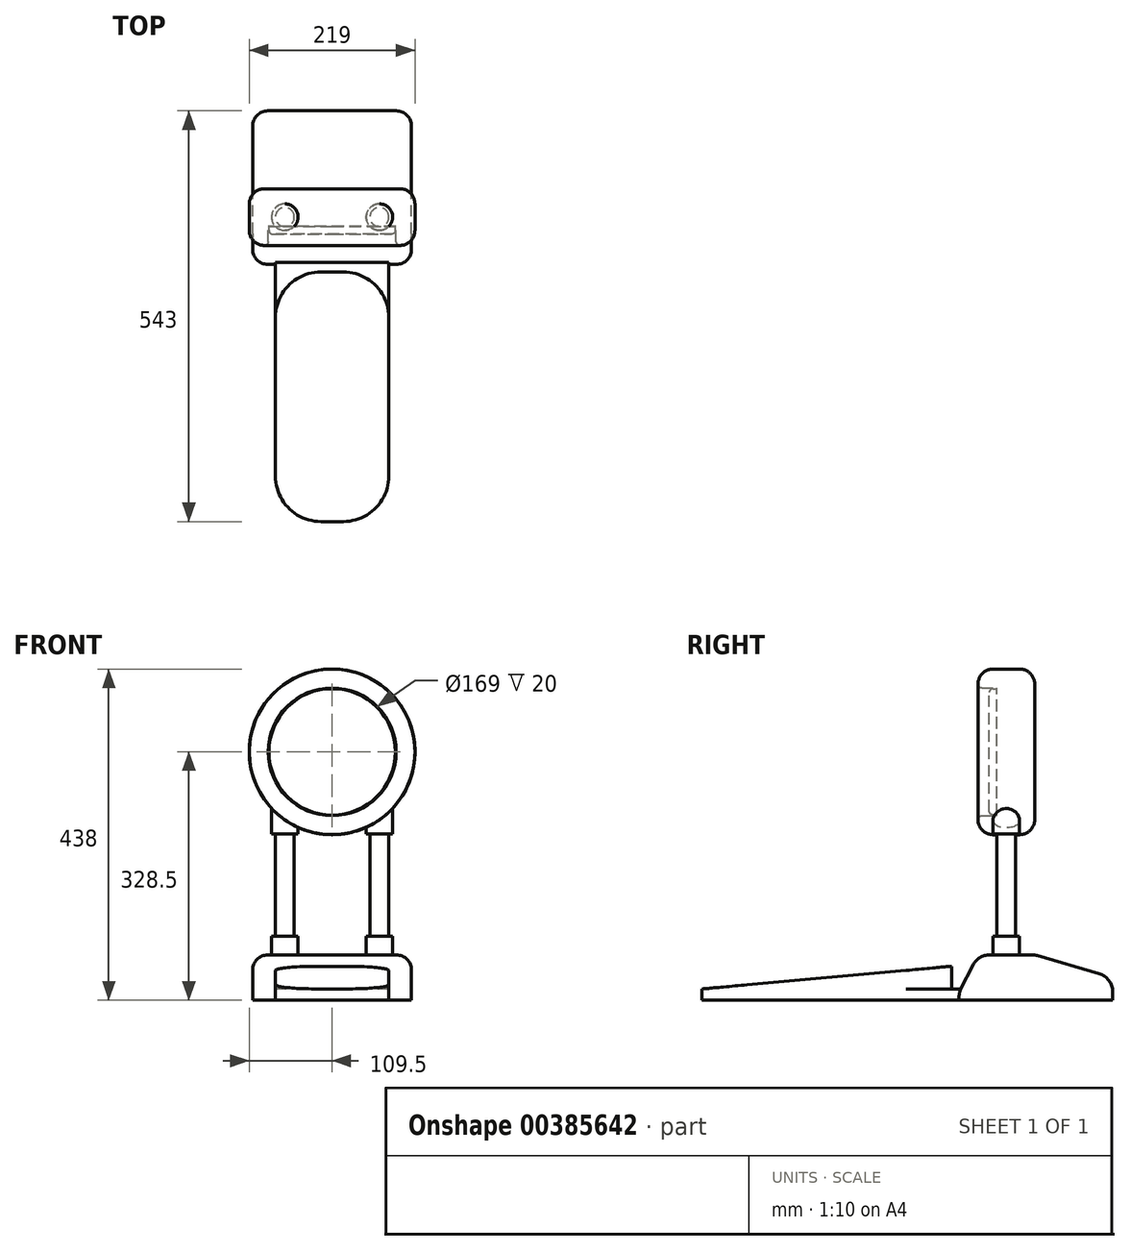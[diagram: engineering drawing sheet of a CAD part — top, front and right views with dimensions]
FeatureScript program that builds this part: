
annotation { "Feature Type Name" : "Feature", "Feature Type Description" : "" }
export const myFeature = defineFeature(function(context is Context, id is Id, definition is map)
    precondition{}
    {
        {
            var Q0;
            Q0=qCreatedBy(makeId("Front.planeOp"),FACE);
            var sketch = newSketch(context, id + "F0", { "sketchPlane" : qUnion([Q0])});
            skLineSegment(sketch, "E0.bottom", {"start": v(-109.5, 0) * mm, "end": v(109.5, 0) * mm, "construction": true});
            skLineSegment(sketch, "E0.top", {"start": v(-109.5, 438) * mm, "end": v(109.5, 438) * mm, "construction": true});
            skLineSegment(sketch, "E0.left", {"start": v(-109.5, 0) * mm, "end": v(-109.5, 438) * mm, "construction": true});
            skLineSegment(sketch, "E0.right", {"start": v(109.5, 0) * mm, "end": v(109.5, 438) * mm, "construction": true});
            skCircle(sketch, "E1", {"center": v(0, 328.5) * mm, "radius": 109.5 * mm});
            skCircle(sketch, "E2", {"center": v(0, 328.5) * mm, "radius": 83.5 * mm});
            skCircle(sketch, "E3", {"center": v(0, 328.5) * mm, "radius": 84.5 * mm});
            skSolve(sketch);
        }
        {
            var Q0;
            Q0=makeQuery(id+"F0.imprint","IMPRINT",FACE,{"disambiguationData":[TD([[makeQuery(id+"F0.imprint","IMPRINT",EDGE,{"derivedFrom":sQuery(id+"F0.wireOp",EDGE,"E1")}),1.0]])]});
            var Q1;
            Q1=makeQuery(id+"F0.imprint","IMPRINT",FACE,{"disambiguationData":[TD([[makeQuery(id+"F0.imprint","IMPRINT",EDGE,{"derivedFrom":sQuery(id+"F0.wireOp",EDGE,"E2")}),1.0]])]});
            var Q2;
            Q2=makeQuery(id+"F0.imprint","IMPRINT",FACE,{"disambiguationData":[TD([[makeQuery(id+"F0.imprint","IMPRINT",EDGE,{"derivedFrom":sQuery(id+"F0.wireOp",EDGE,"E2")}),-1.0]])]});
            extrude(context, id + "F1", {"entities" : qUnion([Q0, Q1, Q2]), "oppositeDirection" : true, "depth" : 50 * mm});
        }
        {
            var Q0;
            Q0=makeQuery(id+"F0.imprint","IMPRINT",FACE,{"disambiguationData":[TD([[makeQuery(id+"F0.imprint","IMPRINT",EDGE,{"derivedFrom":sQuery(id+"F0.wireOp",EDGE,"E2")}),1.0]])]});
            extrude(context, id + "F2", {"entities" : qUnion([Q0]), "operationType" : NewBodyOperationType.ADD, "depth" : 10 * mm});
        }
        {
            var Q0;
            Q0=makeQuery(id+"F0.imprint","IMPRINT",FACE,{"disambiguationData":[TD([[makeQuery(id+"F0.imprint","IMPRINT",EDGE,{"derivedFrom":sQuery(id+"F0.wireOp",EDGE,"E1")}),1.0]])]});
            extrude(context, id + "F3", {"entities" : qUnion([Q0]), "operationType" : NewBodyOperationType.ADD, "depth" : 25 * mm});
        }
        {
            var Q0;
            Q0=makeQuery(id+"F3.opExtrude","CAP_EDGE",EDGE,{"disambiguationData":[OSD([sQuery(id+"F0.wireOp",EDGE,"E1")])],"isStart":false});
            var Q1;
            Q1=makeQuery(id+"F1.opExtrude","CAP_EDGE",EDGE,{"disambiguationData":[OSD([sQuery(id+"F0.wireOp",EDGE,"E1")])],"isStart":false});
            fillet(context, id + "F4", {"entities" : qUnion([Q0, Q1]), "radius" : 20 * mm, "tangentPropagation" : true, "allowEdgeOverflow" : false});
        }
        {
            var Q0;
            Q0=makeQuery(id+"F3.opExtrude","CAP_EDGE",EDGE,{"disambiguationData":[OSD([sQuery(id+"F0.wireOp",EDGE,"E3")])],"isStart":false});
            fillet(context, id + "F5", {"entities" : qUnion([Q0]), "radius" : 5 * mm, "tangentPropagation" : true, "allowEdgeOverflow" : false});
        }
        {
            var Q0;
            Q0=makeQuery(id+"F2.opExtrude","CAP_EDGE",EDGE,{"disambiguationData":[OSD([sQuery(id+"F0.wireOp",EDGE,"E2")])],"isStart":false});
            fillet(context, id + "F6", {"entities" : qUnion([Q0]), "radius" : 5 * mm, "tangentPropagation" : true, "allowEdgeOverflow" : false});
        }
        {
            var Q0;
            Q0=qCreatedBy(makeId("Right.planeOp"),FACE);
            var sketch = newSketch(context, id + "F7", { "sketchPlane" : qUnion([Q0])});
            skLineSegment(sketch, "E4.bottom", {"start": v(-50, 0) * mm, "end": v(153, 0) * mm});
            skLineSegment(sketch, "E4.top", {"start": v(-25, 60) * mm, "end": v(50, 60) * mm});
            skLineSegment(sketch, "E4.left", {"start": v(-50, 0) * mm, "end": v(-50, 10) * mm});
            skLineSegment(sketch, "E4.right", {"start": v(153, 0) * mm, "end": v(153, 30) * mm});
            skLineSegment(sketch, "E5", {"start": v(-50, 10) * mm, "end": v(-25, 60) * mm});
            skLineSegment(sketch, "E6", {"start": v(50, 60) * mm, "end": v(153, 30) * mm});
            skSolve(sketch);
        }
        {
            var Q0;
            Q0=makeQuery(id+"F7.imprint","IMPRINT",FACE,{"disambiguationData":[TD([[makeQuery(id+"F7.imprint","IMPRINT",EDGE,{"derivedFrom":sQuery(id+"F7.wireOp",EDGE,"E4.bottom")}),1.0]])]});
            extrude(context, id + "F8", {"entities" : qUnion([Q0]), "depth" : 105 * mm, "hasSecondDirection" : true, "secondDirectionOppositeDirection" : true, "secondDirectionDepth" : 105 * mm});
        }
        {
            var Q0;
            Q0=makeQuery(id+"F8.opExtrude","SWEPT_FACE",FACE,{"disambiguationData":[OSD([sQuery(id+"F7.wireOp",EDGE,"E4.top")])]});
            var sketch = newSketch(context, id + "F9", { "sketchPlane" : qUnion([Q0])});
            skCircle(sketch, "E7", {"center": v(-62.5, 12.5) * mm, "radius": 17.5 * mm});
            skCircle(sketch, "E8", {"center": v(62.5, 12.5) * mm, "radius": 17.5 * mm});
            skLineSegment(sketch, "E9", {"start": v(-62.5, 12.5) * mm, "end": v(62.5, 12.5) * mm, "construction": true});
            skCircle(sketch, "E10", {"center": v(-62.5, 12.5) * mm, "radius": 12.5 * mm});
            skCircle(sketch, "E11", {"center": v(62.5, 12.5) * mm, "radius": 12.5 * mm});
            skSolve(sketch);
        }
        {
            var Q0;
            Q0=makeQuery(id+"F9.imprint","IMPRINT",FACE,{"disambiguationData":[TD([[makeQuery(id+"F9.imprint","IMPRINT",EDGE,{"derivedFrom":sQuery(id+"F9.wireOp",EDGE,"E11")}),1.0]])]});
            var Q1;
            Q1=makeQuery(id+"F9.imprint","IMPRINT",FACE,{"disambiguationData":[TD([[makeQuery(id+"F9.imprint","IMPRINT",EDGE,{"derivedFrom":sQuery(id+"F9.wireOp",EDGE,"E10")}),1.0]])]});
            var Q2;
            Q2=makeQuery(id+"F1.opExtrude","SWEPT_BODY",BODY,{"disambiguationData":[OSD([sQuery(id+"F0.wireOp",EDGE,"E1")])]});
            extrude(context, id + "F10", {"entities" : qUnion([Q0, Q1]), "operationType" : NewBodyOperationType.ADD, "endBound" : BoundingType.UP_TO_BODY, "endBoundEntityBody" : qUnion([Q2]), "depth" : 25 * mm});
        }
        {
            var Q0;
            Q0=makeQuery(id+"F9.imprint","IMPRINT",FACE,{"disambiguationData":[TD([[makeQuery(id+"F9.imprint","IMPRINT",EDGE,{"derivedFrom":sQuery(id+"F9.wireOp",EDGE,"E8")}),1.0]])]});
            var Q1;
            Q1=makeQuery(id+"F9.imprint","IMPRINT",FACE,{"disambiguationData":[TD([[makeQuery(id+"F9.imprint","IMPRINT",EDGE,{"derivedFrom":sQuery(id+"F9.wireOp",EDGE,"E7")}),1.0]])]});
            extrude(context, id + "F11", {"entities" : qUnion([Q0, Q1]), "operationType" : NewBodyOperationType.ADD, "depth" : 25 * mm});
        }
        {
            var Q0;
            Q0=makeQuery(id+"F9.imprint","IMPRINT",FACE,{"disambiguationData":[TD([[makeQuery(id+"F9.imprint","IMPRINT",EDGE,{"derivedFrom":sQuery(id+"F9.wireOp",EDGE,"E7")}),1.0]])]});
            var Q1;
            Q1=makeQuery(id+"F9.imprint","IMPRINT",FACE,{"disambiguationData":[TD([[makeQuery(id+"F9.imprint","IMPRINT",EDGE,{"derivedFrom":sQuery(id+"F9.wireOp",EDGE,"E8")}),1.0]])]});
            var Q2;
            {var subQ0=sQuery(id+"F0.wireOp",EDGE,"E1");Q2=makeQuery(id+"F3.boolean.opBoolean","MERGE",FACE,{"derivedFrom":[makeQuery(id+"F1.opExtrude","SWEPT_FACE",FACE,{"disambiguationData":[OSD([subQ0])]}),makeQuery(id+"F3.opExtrude","SWEPT_FACE",FACE,{"disambiguationData":[OSD([subQ0])]})]});}
            extrude(context, id + "F12", {"entities" : qUnion([Q0, Q1]), "operationType" : NewBodyOperationType.ADD, "endBound" : BoundingType.UP_TO_SURFACE, "endBoundEntityFace" : qUnion([Q2]), "depth" : 25 * mm, "hasSecondDirection" : true, "secondDirectionOppositeDirection" : false, "secondDirectionDepth" : 160 * mm});
        }
        {
            var Q0;
            Q0=makeQuery(id+"F8.opExtrude","SWEPT_EDGE",EDGE,{"disambiguationData":[OSD([sQuery(id+"F7.wireOp",EDGE,"E4.left"),sQuery(id+"F7.wireOp",EDGE,"E5")])]});
            fillet(context, id + "F13", {"entities" : qUnion([Q0]), "radius" : 25 * mm, "tangentPropagation" : true, "allowEdgeOverflow" : false});
        }
        {
            var Q0;
            Q0=makeQuery(id+"F8.opExtrude","SWEPT_EDGE",EDGE,{"disambiguationData":[OSD([sQuery(id+"F7.wireOp",EDGE,"E4.top"),sQuery(id+"F7.wireOp",EDGE,"E5")])]});
            var Q1;
            Q1=makeQuery(id+"F8.opExtrude","SWEPT_EDGE",EDGE,{"disambiguationData":[OSD([sQuery(id+"F7.wireOp",EDGE,"E4.top"),sQuery(id+"F7.wireOp",EDGE,"E6")])]});
            fillet(context, id + "F14", {"entities" : qUnion([Q0, Q1]), "radius" : 25 * mm, "tangentPropagation" : true, "allowEdgeOverflow" : false});
        }
        {
            var Q0;
            Q0=makeQuery(id+"F8.opExtrude","SWEPT_EDGE",EDGE,{"disambiguationData":[OSD([sQuery(id+"F7.wireOp",EDGE,"E4.right"),sQuery(id+"F7.wireOp",EDGE,"E6")])]});
            fillet(context, id + "F15", {"entities" : qUnion([Q0]), "radius" : 25 * mm, "tangentPropagation" : true, "allowEdgeOverflow" : false});
        }
        {
            var Q0;
            Q0=makeQuery(id+"F8.opExtrude","CAP_EDGE",EDGE,{"disambiguationData":[OSD([sQuery(id+"F7.wireOp",EDGE,"E5")])],"isStart":false});
            var Q1;
            Q1=makeQuery(id+"F8.opExtrude","CAP_EDGE",EDGE,{"disambiguationData":[OSD([sQuery(id+"F7.wireOp",EDGE,"E5")])],"isStart":true});
            fillet(context, id + "F16", {"entities" : qUnion([Q0, Q1]), "radius" : 20 * mm, "tangentPropagation" : true, "allowEdgeOverflow" : false});
        }
        {
            var Q0;
            Q0=qCreatedBy(makeId("Right.planeOp"),FACE);
            var sketch = newSketch(context, id + "F17", { "sketchPlane" : qUnion([Q0])});
            skLineSegment(sketch, "E12", {"start": v(-30, 0) * mm, "end": v(-390, 0) * mm});
            skLineSegment(sketch, "E13", {"start": v(-390, 0) * mm, "end": v(-390, 15) * mm});
            skLineSegment(sketch, "E14", {"start": v(-390, 15) * mm, "end": v(-60, 45) * mm});
            skLineSegment(sketch, "E15", {"start": v(-60, 45) * mm, "end": v(-60, 15) * mm});
            skLineSegment(sketch, "E16", {"start": v(-60, 15) * mm, "end": v(-30, 15) * mm});
            skLineSegment(sketch, "E17", {"start": v(-30, 15) * mm, "end": v(-30, 0) * mm});
            skLineSegment(sketch, "E18", {"start": v(-60, 45) * mm, "end": v(-30, 45) * mm, "construction": true});
            skSolve(sketch);
        }
        {
            var Q0;
            Q0=makeQuery(id+"F17.imprint","IMPRINT",FACE,{"disambiguationData":[TD([[makeQuery(id+"F17.imprint","IMPRINT",EDGE,{"derivedFrom":sQuery(id+"F17.wireOp",EDGE,"E12")}),-1.0]])]});
            extrude(context, id + "F18", {"entities" : qUnion([Q0]), "operationType" : NewBodyOperationType.ADD, "depth" : 75 * mm, "hasSecondDirection" : true, "secondDirectionOppositeDirection" : true, "secondDirectionDepth" : 75 * mm});
        }
        {
            var Q0;
            Q0=makeQuery(id+"F18.opExtrude","CAP_EDGE",EDGE,{"disambiguationData":[OSD([sQuery(id+"F17.wireOp",EDGE,"E13")])],"isStart":false});
            var Q1;
            Q1=makeQuery(id+"F18.opExtrude","CAP_EDGE",EDGE,{"disambiguationData":[OSD([sQuery(id+"F17.wireOp",EDGE,"E13")])],"isStart":true});
            var Q2;
            Q2=makeQuery(id+"F18.opExtrude","CAP_EDGE",EDGE,{"disambiguationData":[OSD([sQuery(id+"F17.wireOp",EDGE,"E15")])],"isStart":false});
            var Q3;
            Q3=makeQuery(id+"F18.opExtrude","CAP_EDGE",EDGE,{"disambiguationData":[OSD([sQuery(id+"F17.wireOp",EDGE,"E15")])],"isStart":true});
            fillet(context, id + "F19", {"entities" : qUnion([Q0, Q1, Q2, Q3]), "radius" : 60 * mm, "tangentPropagation" : true, "allowEdgeOverflow" : false});
        }
    });
